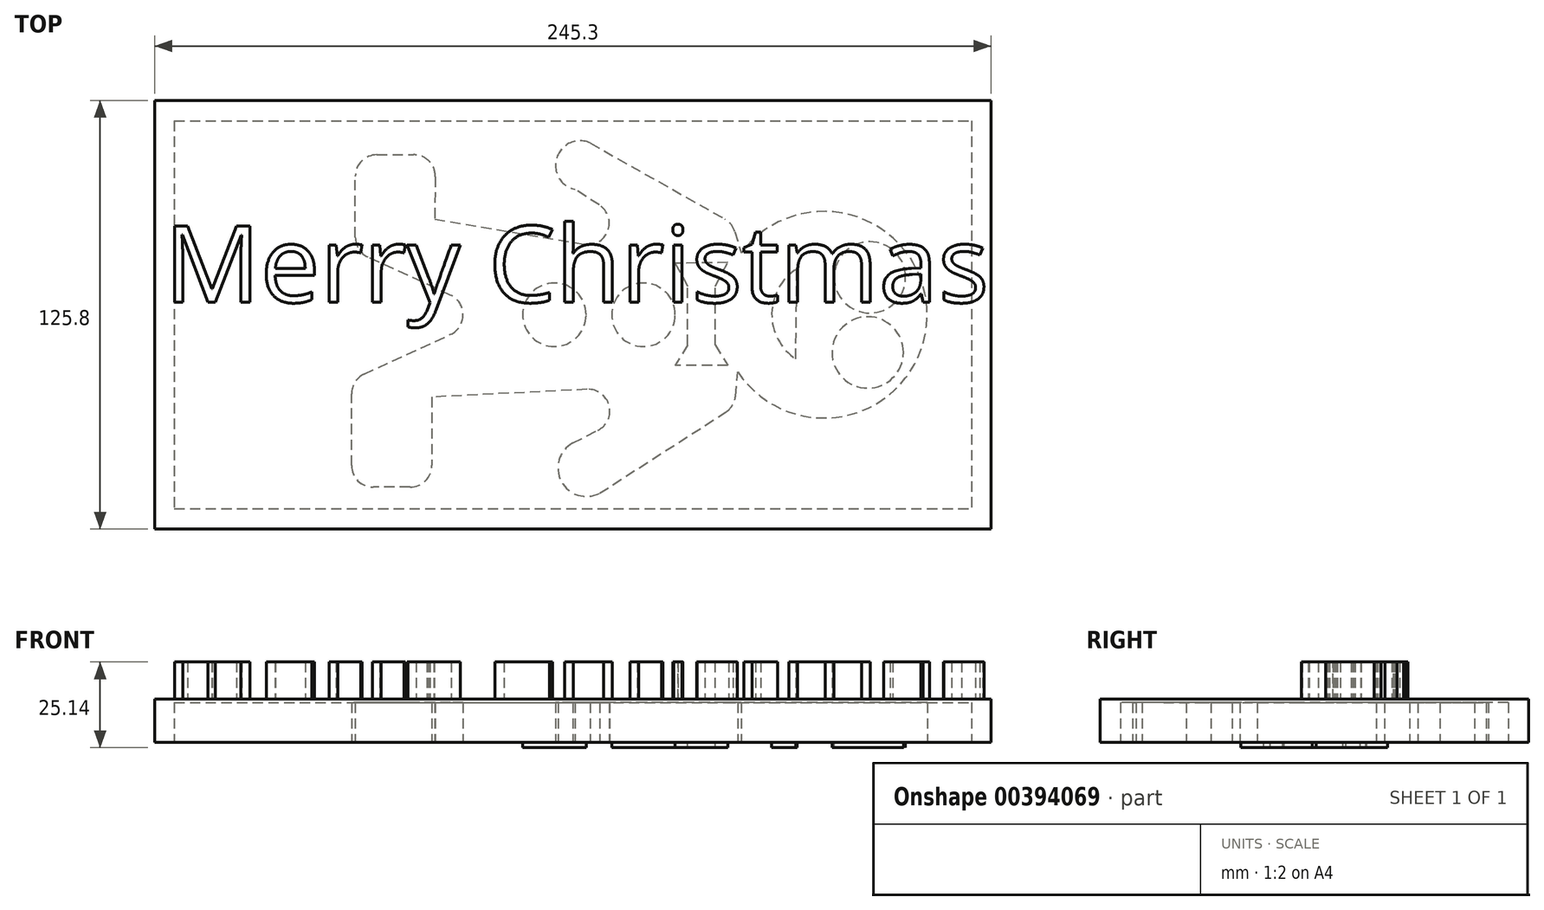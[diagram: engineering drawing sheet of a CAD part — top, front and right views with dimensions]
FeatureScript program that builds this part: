
annotation { "Feature Type Name" : "Feature", "Feature Type Description" : "" }
export const myFeature = defineFeature(function(context is Context, id is Id, definition is map)
    precondition{}
    {
        {
            var Q0;
            Q0=qCreatedBy(makeId("Top.planeOp"),FACE);
            var sketch = newSketch(context, id + "F0", { "sketchPlane" : qUnion([Q0])});
            skLineSegment(sketch, "E0.bottom", {"start": v(-122.65, 62.9) * mm, "end": v(122.65, 62.9) * mm});
            skLineSegment(sketch, "E0.top", {"start": v(-122.65, -62.9) * mm, "end": v(122.65, -62.9) * mm});
            skLineSegment(sketch, "E0.left", {"start": v(-122.65, 62.9) * mm, "end": v(-122.65, -62.9) * mm});
            skLineSegment(sketch, "E0.right", {"start": v(122.65, 62.9) * mm, "end": v(122.65, -62.9) * mm});
            skPoint(sketch, "E0.middle", {"position": v(0, 0) * mm});
            skSolve(sketch);
        }
        {
            var Q0;
            Q0 = qSketchRegion(id + "F0", true);
            extrude(context, id + "F1", {"entities" : qUnion([Q0]), "depth" : 12.7 * mm});
        }
        {
            var Q0;
            Q0=qCreatedBy(makeId("Top.planeOp"),FACE);
            var sketch = newSketch(context, id + "F2", { "sketchPlane" : qUnion([Q0])});
            skLineSegment(sketch, "E1.bottom", {"start": v(-116.92, 56.88) * mm, "end": v(116.92, 56.88) * mm});
            skLineSegment(sketch, "E1.top", {"start": v(-116.92, -56.88) * mm, "end": v(116.92, -56.88) * mm});
            skLineSegment(sketch, "E1.left", {"start": v(-116.92, 56.88) * mm, "end": v(-116.92, -56.88) * mm});
            skLineSegment(sketch, "E1.right", {"start": v(116.92, 56.88) * mm, "end": v(116.92, -56.88) * mm});
            skPoint(sketch, "E1.middle", {"position": v(0, 0) * mm});
            skSolve(sketch);
        }
        {
            var Q0;
            Q0 = qSketchRegion(id + "F2", true);
            extrude(context, id + "F3", {"entities" : qUnion([Q0]), "operationType" : NewBodyOperationType.REMOVE, "depth" : 11.68 * mm});
        }
        {
            var Q0;
            Q0=qCreatedBy(makeId("Top.planeOp"),FACE);
            var sketch = newSketch(context, id + "F4", { "sketchPlane" : qUnion([Q0])});
            skCircle(sketch, "E2", {"center": v(73.65, 0) * mm, "radius": 30.3 * mm});
            skLineSegment(sketch, "E3.left", {"start": v(0, 0) * mm, "end": v(0, 0) * mm});
            skArc(sketch, "E4", {"start": v(0, -37.64) * mm, "mid": v(-3.4, -48.9) * mm, "end": v(7.84, -52.36) * mm});
            skLineSegment(sketch, "E5", {"start": v(0, -37.64) * mm, "end": v(7.37, -33.9) * mm});
            skLineSegment(sketch, "E6", {"start": v(4.18, -21.9) * mm, "end": v(-41.38, -24.15) * mm});
            skLineSegment(sketch, "E7", {"start": v(3.28, 20.6) * mm, "end": v(-40.53, 27.97) * mm});
            skLineSegment(sketch, "E8", {"start": v(7.77, 32.2) * mm, "end": v(0.63, 36.79) * mm});
            skArc(sketch, "E9", {"start": v(5.12, 50.38) * mm, "mid": v(-4.74, 46.1) * mm, "end": v(0.63, 36.79) * mm});
            skLineSegment(sketch, "E10", {"start": v(-41.38, -24.15) * mm, "end": v(-41.38, -44.25) * mm});
            skLineSegment(sketch, "E11", {"start": v(-47.73, -50.6) * mm, "end": v(-58.6, -50.6) * mm});
            skLineSegment(sketch, "E12", {"start": v(-64.94, -44.25) * mm, "end": v(-64.94, -23.21) * mm});
            skLineSegment(sketch, "E13", {"start": v(-61.25, -17.45) * mm, "end": v(-35.9, -5.76) * mm});
            skLineSegment(sketch, "E14", {"start": v(-35.9, 5.77) * mm, "end": v(-60.14, 16.98) * mm});
            skLineSegment(sketch, "E15", {"start": v(-63.83, 22.74) * mm, "end": v(-63.83, 40.6) * mm});
            skLineSegment(sketch, "E16", {"start": v(-57.48, 46.95) * mm, "end": v(-46.7, 46.95) * mm});
            skLineSegment(sketch, "E17", {"start": v(-40.34, 40.51) * mm, "end": v(-40.53, 27.97) * mm});
            skPoint(sketch, "E18.visualSharp", {"position": v(-41.38, -50.6) * mm});
            skArc(sketch, "E18.filletArc", {"start": v(-47.73, -50.6) * mm, "mid": v(-43.24, -48.74) * mm, "end": v(-41.38, -44.25) * mm});
            skPoint(sketch, "E19.visualSharp", {"position": v(-64.94, -50.6) * mm});
            skArc(sketch, "E19.filletArc", {"start": v(-64.94, -44.25) * mm, "mid": v(-63.08, -48.74) * mm, "end": v(-58.6, -50.6) * mm});
            skPoint(sketch, "E20.visualSharp", {"position": v(-64.94, -19.15) * mm});
            skArc(sketch, "E20.filletArc", {"start": v(-61.25, -17.45) * mm, "mid": v(-63.94, -19.79) * mm, "end": v(-64.94, -23.21) * mm});
            skPoint(sketch, "E21.visualSharp", {"position": v(-23.4, 0) * mm});
            skArc(sketch, "E21.filletArc", {"start": v(-35.9, -5.76) * mm, "mid": v(-32.2, 0) * mm, "end": v(-35.9, 5.77) * mm});
            skPoint(sketch, "E22.visualSharp", {"position": v(-63.83, 18.68) * mm});
            skArc(sketch, "E22.filletArc", {"start": v(-63.83, 22.74) * mm, "mid": v(-62.83, 19.32) * mm, "end": v(-60.14, 16.98) * mm});
            skPoint(sketch, "E23.visualSharp", {"position": v(-63.83, 46.95) * mm});
            skArc(sketch, "E23.filletArc", {"start": v(-57.48, 46.95) * mm, "mid": v(-61.97, 45.1) * mm, "end": v(-63.83, 40.6) * mm});
            skPoint(sketch, "E24.visualSharp", {"position": v(-40.25, 46.95) * mm});
            skArc(sketch, "E24.filletArc", {"start": v(-40.34, 40.51) * mm, "mid": v(-42.17, 45.06) * mm, "end": v(-46.7, 46.95) * mm});
            skPoint(sketch, "E25.visualSharp", {"position": v(33.87, -20.42) * mm});
            skArc(sketch, "E25.filletArc", {"start": v(7.37, -33.9) * mm, "mid": v(10.63, -26.6) * mm, "end": v(4.18, -21.9) * mm});
            skPoint(sketch, "E26.visualSharp", {"position": v(33.87, 15.46) * mm});
            skArc(sketch, "E26.filletArc", {"start": v(3.28, 20.6) * mm, "mid": v(10.26, 24.58) * mm, "end": v(7.77, 32.2) * mm});
            skLineSegment(sketch, "E27", {"start": v(7.84, -52.36) * mm, "end": v(44.81, -28.62) * mm});
            skLineSegment(sketch, "E28", {"start": v(5.12, 50.38) * mm, "end": v(44.54, 28.13) * mm});
            skLineSegment(sketch, "E29", {"start": v(47.7, -23.9) * mm, "end": v(48.4, -16.74) * mm});
            skLineSegment(sketch, "E30", {"start": v(47.5, 24.4) * mm, "end": v(49.37, 18.14) * mm});
            skPoint(sketch, "E31.visualSharp", {"position": v(47.4, -26.96) * mm});
            skArc(sketch, "E31.filletArc", {"start": v(44.81, -28.62) * mm, "mid": v(46.8, -26.59) * mm, "end": v(47.7, -23.9) * mm});
            skPoint(sketch, "E32.visualSharp", {"position": v(46.77, 26.87) * mm});
            skArc(sketch, "E32.filletArc", {"start": v(47.5, 24.4) * mm, "mid": v(46.38, 26.55) * mm, "end": v(44.54, 28.13) * mm});
            skPoint(sketch, "E33.newPointA", {"position": v(-41.38, -34.2) * mm});
            skPoint(sketch, "E33.newPointB", {"position": v(-40.43, 34.24) * mm});
            skSolve(sketch);
        }
        {
            var Q0;
            Q0 = qSketchRegion(id + "F4", true);
            extrude(context, id + "F5", {"entities" : qUnion([Q0]), "operationType" : NewBodyOperationType.ADD, "depth" : 12.7 * mm});
        }
        {
            var Q0;
            Q0=qCreatedBy(makeId("Top.planeOp"),FACE);
            var sketch = newSketch(context, id + "F6", { "sketchPlane" : qUnion([Q0])});
            skCircle(sketch, "E34", {"center": v(86.5, -11.08) * mm, "radius": 10.47 * mm});
            skCircle(sketch, "E35", {"center": v(87.13, 10.96) * mm, "radius": 10.47 * mm});
            skArc(sketch, "E36", {"start": v(65.73, 13.47) * mm, "mid": v(58.35, 0.34) * mm, "end": v(65.41, -12.97) * mm});
            skLineSegment(sketch, "E37", {"start": v(65.41, -12.97) * mm, "end": v(65.73, 13.47) * mm});
            skLineSegment(sketch, "E38.bottom", {"start": v(41.8, -8.87) * mm, "end": v(33.62, -8.87) * mm});
            skLineSegment(sketch, "E38.top", {"start": v(41.8, 8.44) * mm, "end": v(33.62, 8.44) * mm});
            skLineSegment(sketch, "E38.left", {"start": v(41.8, -8.87) * mm, "end": v(41.8, 8.44) * mm});
            skLineSegment(sketch, "E38.right", {"start": v(33.62, -8.87) * mm, "end": v(33.62, 8.44) * mm});
            skLineSegment(sketch, "E39", {"start": v(41.8, -8.87) * mm, "end": v(45.44, -14.87) * mm});
            skLineSegment(sketch, "E40", {"start": v(45.44, -14.87) * mm, "end": v(30.02, -14.87) * mm});
            skLineSegment(sketch, "E41", {"start": v(45.44, 15.35) * mm, "end": v(30.02, 15.07) * mm});
            skLineSegment(sketch, "E42", {"start": v(30.02, 15.07) * mm, "end": v(33.62, 8.44) * mm});
            skCircle(sketch, "E43", {"center": v(20.72, 0) * mm, "radius": 9.31 * mm});
            skCircle(sketch, "E44", {"center": v(-5.4, 0) * mm, "radius": 9.31 * mm});
            skLineSegment(sketch, "E45", {"start": v(33.62, -8.87) * mm, "end": v(30.02, -14.87) * mm});
            skLineSegment(sketch, "E46", {"start": v(41.8, 8.44) * mm, "end": v(45.44, 15.35) * mm});
            skSolve(sketch);
        }
        {
            var Q0;
            Q0 = qSketchRegion(id + "F6", true);
            extrude(context, id + "F7", {"entities" : qUnion([Q0]), "operationType" : NewBodyOperationType.ADD, "oppositeDirection" : true, "depth" : 1.52 * mm});
        }
        {
            var Q0;
            Q0 = qSketchRegion(id + "F6", true);
            extrude(context, id + "F8", {"entities" : qUnion([Q0]), "operationType" : NewBodyOperationType.ADD, "oppositeDirection" : true, "depth" : 1.27 * mm});
        }
        {
            var Q0;
            Q0=makeQuery(id+"F1.opExtrude","CAP_FACE",FACE,{"disambiguationData":[OSD([sQuery(id+"F0.wireOp",EDGE,"E0.bottom"),sQuery(id+"F0.wireOp",EDGE,"E0.top"),sQuery(id+"F0.wireOp",EDGE,"E0.left"),sQuery(id+"F0.wireOp",EDGE,"E0.right")])],"isStart":false});
            var sketch = newSketch(context, id + "F9", { "sketchPlane" : qUnion([Q0])});
            skText(sketch, "E47", { "text": "Merry Christmas ", "fontName": "OpenSans-Regular.ttf"});
            const initialGuessF9  = {"E47": [-0.11994, 0.00367, 1, 0, 0.0225]};
            skSetInitialGuess(sketch, initialGuessF9);
            skSolve(sketch);
        }
        {
            var Q0;
            Q0 = qSketchRegion(id + "F9", true);
            extrude(context, id + "F10", {"entities" : qUnion([Q0]), "operationType" : NewBodyOperationType.ADD, "depth" : 10.92 * mm});
        }
    });
